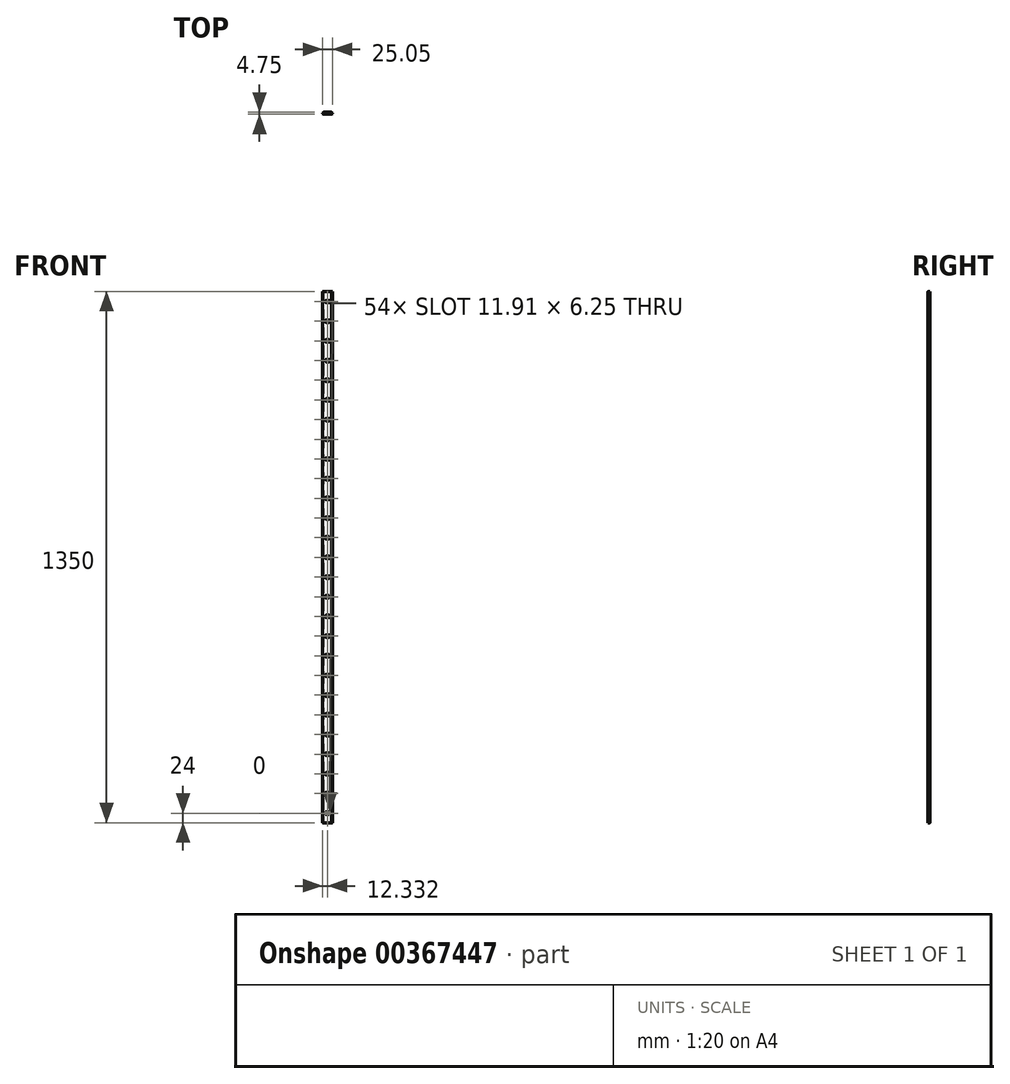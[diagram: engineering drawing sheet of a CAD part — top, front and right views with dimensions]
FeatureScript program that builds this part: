
annotation { "Feature Type Name" : "Feature", "Feature Type Description" : "" }
export const myFeature = defineFeature(function(context is Context, id is Id, definition is map)
    precondition{}
    {
        {
            var Q0;
            Q0=qCreatedBy(makeId("Top.planeOp"),FACE);
            var sketch = newSketch(context, id + "F0", { "sketchPlane" : qUnion([Q0])});
            skLineSegment(sketch, "E0", {"start": v(0, 0) * mm, "end": v(20.12, 0) * mm});
            skLineSegment(sketch, "E1", {"start": v(20.12, 0) * mm, "end": v(22.5, -2.37) * mm});
            skLineSegment(sketch, "E2", {"start": v(22.5, -2.37) * mm, "end": v(20.12, -4.75) * mm});
            skLineSegment(sketch, "E3", {"start": v(20.12, -4.75) * mm, "end": v(19.53, -4.75) * mm});
            skLineSegment(sketch, "E4", {"start": v(19.53, -4.75) * mm, "end": v(19.53, -2.37) * mm});
            skLineSegment(sketch, "E5", {"start": v(19.53, -2.37) * mm, "end": v(0, -2.38) * mm});
            skLineSegment(sketch, "E6", {"start": v(0, -2.38) * mm, "end": v(0, 0) * mm});
            skSolve(sketch);
        }
        {
            var Q0;
            Q0=qSketchRegion(id+"F0",true);
            extrude(context, id + "F1", {"entities" : qUnion([Q0]), "depth" : 1350 * mm});
        }
        {
            var Q0;
            Q0=makeQuery(id+"F1.opExtrude","SWEPT_EDGE",EDGE,{"disambiguationData":[OSD([sQuery(id+"F0.wireOp",EDGE,"E2"),sQuery(id+"F0.wireOp",EDGE,"E3")])]});
            var Q1;
            Q1=makeQuery(id+"F1.opExtrude","SWEPT_EDGE",EDGE,{"disambiguationData":[OSD([sQuery(id+"F0.wireOp",EDGE,"E1"),sQuery(id+"F0.wireOp",EDGE,"E2")])]});
            var Q2;
            Q2=makeQuery(id+"F1.opExtrude","SWEPT_EDGE",EDGE,{"disambiguationData":[OSD([sQuery(id+"F0.wireOp",EDGE,"E0"),sQuery(id+"F0.wireOp",EDGE,"E1")])]});
            fillet(context, id + "F2", {"entities" : qUnion([Q0, Q1, Q2]), "radius" : 0.5 * mm, "tangentPropagation" : true, "allowEdgeOverflow" : false});
        }
        {
            var Q0;
            Q0=makeQuery(id+"F1.opExtrude","SWEPT_BODY",BODY,{"disambiguationData":[OSD([sQuery(id+"F0.wireOp",EDGE,"E0"),sQuery(id+"F0.wireOp",EDGE,"E1"),sQuery(id+"F0.wireOp",EDGE,"E2"),sQuery(id+"F0.wireOp",EDGE,"E3"),sQuery(id+"F0.wireOp",EDGE,"E4"),sQuery(id+"F0.wireOp",EDGE,"E5"),sQuery(id+"F0.wireOp",EDGE,"E6")])]});
            var Q1;
            Q1=makeQuery(id+"F1.opExtrude","SWEPT_EDGE",EDGE,{"disambiguationData":[OSD([sQuery(id+"F0.wireOp",EDGE,"E5"),sQuery(id+"F0.wireOp",EDGE,"E6")])]});
            transform(context, id + "F3", {"entities" : qUnion([Q0]), "transformType" : TransformType.ROTATION, "transformAxis" : qUnion([Q1]), "angle" : 180 * degree, "makeCopy" : true});
        }
        {
            var Q0;
            Q0=makeQuery(id+"F3.opPattern","COPY",BODY,{"derivedFrom":makeQuery(id+"F1.opExtrude","SWEPT_BODY",BODY,{"disambiguationData":[OSD([sQuery(id+"F0.wireOp",EDGE,"E0"),sQuery(id+"F0.wireOp",EDGE,"E1"),sQuery(id+"F0.wireOp",EDGE,"E2"),sQuery(id+"F0.wireOp",EDGE,"E3"),sQuery(id+"F0.wireOp",EDGE,"E4"),sQuery(id+"F0.wireOp",EDGE,"E5"),sQuery(id+"F0.wireOp",EDGE,"E6")])]}),"instanceName":"1"});
            var Q1;
            Q1=makeQuery(id+"F3.opPattern","COPY",EDGE,{"derivedFrom":makeQuery(id+"F1.opExtrude","CAP_EDGE",EDGE,{"disambiguationData":[OSD([sQuery(id+"F0.wireOp",EDGE,"E5")])],"isStart":true}),"instanceName":"1"});
            transform(context, id + "F4", {"entities" : qUnion([Q0]), "transformType" : TransformType.TRANSLATION_ENTITY, "oppositeDirectionEntity" : false, "transformLine" : qUnion([Q1]), "makeCopy" : false});
        }
        {
            var Q0;
            Q0=makeQuery(id+"F3.opPattern","COPY",FACE,{"derivedFrom":makeQuery(id+"F1.opExtrude","SWEPT_FACE",FACE,{"disambiguationData":[OSD([sQuery(id+"F0.wireOp",EDGE,"E0")])]}),"instanceName":"1"});
            var sketch = newSketch(context, id + "F5", { "sketchPlane" : qUnion([Q0])});
            skLineSegment(sketch, "E7", {"start": v(9.57, 1350) * mm, "end": v(9.57, 1284.45) * mm, "construction": true});
            skLineSegment(sketch, "E8", {"start": v(-9.43, 1324) * mm, "end": v(34.24, 1324) * mm, "construction": true});
            skArc(sketch, "E9", {"start": v(9.57, 1322.68) * mm, "mid": v(15.04, 1322.32) * mm, "end": v(12.4, 1327.12) * mm});
            skArc(sketch, "E10", {"start": v(6.74, 1327.12) * mm, "mid": v(4.1, 1322.32) * mm, "end": v(9.57, 1322.68) * mm});
            skLineSegment(sketch, "E11", {"start": v(12.4, 1320.88) * mm, "end": v(6.74, 1320.88) * mm});
            skLineSegment(sketch, "E12", {"start": v(12.4, 1327.12) * mm, "end": v(6.74, 1327.12) * mm});
            skArc(sketch, "E13.0.1.0", {"start": v(6.74, 1277.12) * mm, "mid": v(4.1, 1272.32) * mm, "end": v(9.57, 1272.68) * mm});
            skLineSegment(sketch, "E13.0.1.1", {"start": v(12.4, 1270.88) * mm, "end": v(6.74, 1270.88) * mm});
            skArc(sketch, "E13.0.1.2", {"start": v(9.57, 1272.68) * mm, "mid": v(15.04, 1272.32) * mm, "end": v(12.4, 1277.12) * mm});
            skLineSegment(sketch, "E13.0.1.3", {"start": v(12.4, 1277.12) * mm, "end": v(6.74, 1277.12) * mm});
            skArc(sketch, "E13.0.2.0", {"start": v(6.74, 1227.13) * mm, "mid": v(4.1, 1222.32) * mm, "end": v(9.57, 1222.68) * mm});
            skLineSegment(sketch, "E13.0.2.1", {"start": v(12.4, 1220.88) * mm, "end": v(6.74, 1220.88) * mm});
            skArc(sketch, "E13.0.2.2", {"start": v(9.57, 1222.68) * mm, "mid": v(15.04, 1222.32) * mm, "end": v(12.4, 1227.13) * mm});
            skLineSegment(sketch, "E13.0.2.3", {"start": v(12.4, 1227.13) * mm, "end": v(6.74, 1227.13) * mm});
            skArc(sketch, "E13.0.3.0", {"start": v(6.74, 1177.13) * mm, "mid": v(4.1, 1172.32) * mm, "end": v(9.57, 1172.68) * mm});
            skLineSegment(sketch, "E13.0.3.1", {"start": v(12.4, 1170.88) * mm, "end": v(6.74, 1170.88) * mm});
            skArc(sketch, "E13.0.3.2", {"start": v(9.57, 1172.68) * mm, "mid": v(15.04, 1172.32) * mm, "end": v(12.4, 1177.13) * mm});
            skLineSegment(sketch, "E13.0.3.3", {"start": v(12.4, 1177.13) * mm, "end": v(6.74, 1177.13) * mm});
            skArc(sketch, "E13.0.4.0", {"start": v(6.74, 1127.13) * mm, "mid": v(4.1, 1122.32) * mm, "end": v(9.57, 1122.68) * mm});
            skLineSegment(sketch, "E13.0.4.1", {"start": v(12.4, 1120.88) * mm, "end": v(6.74, 1120.88) * mm});
            skArc(sketch, "E13.0.4.2", {"start": v(9.57, 1122.68) * mm, "mid": v(15.04, 1122.32) * mm, "end": v(12.4, 1127.13) * mm});
            skLineSegment(sketch, "E13.0.4.3", {"start": v(12.4, 1127.13) * mm, "end": v(6.74, 1127.13) * mm});
            skArc(sketch, "E13.0.5.0", {"start": v(6.74, 1077.13) * mm, "mid": v(4.1, 1072.32) * mm, "end": v(9.57, 1072.68) * mm});
            skLineSegment(sketch, "E13.0.5.1", {"start": v(12.4, 1070.88) * mm, "end": v(6.74, 1070.88) * mm});
            skArc(sketch, "E13.0.5.2", {"start": v(9.57, 1072.68) * mm, "mid": v(15.04, 1072.32) * mm, "end": v(12.4, 1077.13) * mm});
            skLineSegment(sketch, "E13.0.5.3", {"start": v(12.4, 1077.13) * mm, "end": v(6.74, 1077.13) * mm});
            skArc(sketch, "E13.0.6.0", {"start": v(6.74, 1027.13) * mm, "mid": v(4.1, 1022.32) * mm, "end": v(9.57, 1022.68) * mm});
            skLineSegment(sketch, "E13.0.6.1", {"start": v(12.4, 1020.88) * mm, "end": v(6.74, 1020.88) * mm});
            skArc(sketch, "E13.0.6.2", {"start": v(9.57, 1022.68) * mm, "mid": v(15.04, 1022.32) * mm, "end": v(12.4, 1027.13) * mm});
            skLineSegment(sketch, "E13.0.6.3", {"start": v(12.4, 1027.13) * mm, "end": v(6.74, 1027.13) * mm});
            skArc(sketch, "E13.0.7.0", {"start": v(6.74, 977.13) * mm, "mid": v(4.1, 972.32) * mm, "end": v(9.57, 972.68) * mm});
            skLineSegment(sketch, "E13.0.7.1", {"start": v(12.4, 970.88) * mm, "end": v(6.74, 970.88) * mm});
            skArc(sketch, "E13.0.7.2", {"start": v(9.57, 972.68) * mm, "mid": v(15.04, 972.32) * mm, "end": v(12.4, 977.13) * mm});
            skLineSegment(sketch, "E13.0.7.3", {"start": v(12.4, 977.13) * mm, "end": v(6.74, 977.13) * mm});
            skArc(sketch, "E13.0.8.0", {"start": v(6.74, 927.13) * mm, "mid": v(4.1, 922.32) * mm, "end": v(9.57, 922.68) * mm});
            skLineSegment(sketch, "E13.0.8.1", {"start": v(12.4, 920.88) * mm, "end": v(6.74, 920.88) * mm});
            skArc(sketch, "E13.0.8.2", {"start": v(9.57, 922.68) * mm, "mid": v(15.04, 922.32) * mm, "end": v(12.4, 927.13) * mm});
            skLineSegment(sketch, "E13.0.8.3", {"start": v(12.4, 927.13) * mm, "end": v(6.74, 927.13) * mm});
            skArc(sketch, "E13.0.9.0", {"start": v(6.74, 877.13) * mm, "mid": v(4.1, 872.32) * mm, "end": v(9.57, 872.68) * mm});
            skLineSegment(sketch, "E13.0.9.1", {"start": v(12.4, 870.88) * mm, "end": v(6.74, 870.88) * mm});
            skArc(sketch, "E13.0.9.2", {"start": v(9.57, 872.68) * mm, "mid": v(15.04, 872.32) * mm, "end": v(12.4, 877.13) * mm});
            skLineSegment(sketch, "E13.0.9.3", {"start": v(12.4, 877.13) * mm, "end": v(6.74, 877.13) * mm});
            skArc(sketch, "E13.0.10.0", {"start": v(6.74, 827.13) * mm, "mid": v(4.1, 822.32) * mm, "end": v(9.57, 822.68) * mm});
            skLineSegment(sketch, "E13.0.10.1", {"start": v(12.4, 820.88) * mm, "end": v(6.74, 820.88) * mm});
            skArc(sketch, "E13.0.10.2", {"start": v(9.57, 822.68) * mm, "mid": v(15.04, 822.32) * mm, "end": v(12.4, 827.13) * mm});
            skLineSegment(sketch, "E13.0.10.3", {"start": v(12.4, 827.13) * mm, "end": v(6.74, 827.13) * mm});
            skArc(sketch, "E13.0.11.0", {"start": v(6.74, 777.13) * mm, "mid": v(4.1, 772.32) * mm, "end": v(9.57, 772.68) * mm});
            skLineSegment(sketch, "E13.0.11.1", {"start": v(12.4, 770.88) * mm, "end": v(6.74, 770.88) * mm});
            skArc(sketch, "E13.0.11.2", {"start": v(9.57, 772.68) * mm, "mid": v(15.04, 772.32) * mm, "end": v(12.4, 777.13) * mm});
            skLineSegment(sketch, "E13.0.11.3", {"start": v(12.4, 777.13) * mm, "end": v(6.74, 777.13) * mm});
            skArc(sketch, "E13.0.12.0", {"start": v(6.74, 727.13) * mm, "mid": v(4.1, 722.32) * mm, "end": v(9.57, 722.68) * mm});
            skLineSegment(sketch, "E13.0.12.1", {"start": v(12.4, 720.88) * mm, "end": v(6.74, 720.88) * mm});
            skArc(sketch, "E13.0.12.2", {"start": v(9.57, 722.68) * mm, "mid": v(15.04, 722.32) * mm, "end": v(12.4, 727.13) * mm});
            skLineSegment(sketch, "E13.0.12.3", {"start": v(12.4, 727.13) * mm, "end": v(6.74, 727.13) * mm});
            skArc(sketch, "E13.0.13.0", {"start": v(6.74, 677.13) * mm, "mid": v(4.1, 672.32) * mm, "end": v(9.57, 672.68) * mm});
            skLineSegment(sketch, "E13.0.13.1", {"start": v(12.4, 670.88) * mm, "end": v(6.74, 670.88) * mm});
            skArc(sketch, "E13.0.13.2", {"start": v(9.57, 672.68) * mm, "mid": v(15.04, 672.32) * mm, "end": v(12.4, 677.13) * mm});
            skLineSegment(sketch, "E13.0.13.3", {"start": v(12.4, 677.13) * mm, "end": v(6.74, 677.13) * mm});
            skArc(sketch, "E13.0.14.0", {"start": v(6.74, 627.13) * mm, "mid": v(4.1, 622.32) * mm, "end": v(9.57, 622.68) * mm});
            skLineSegment(sketch, "E13.0.14.1", {"start": v(12.4, 620.88) * mm, "end": v(6.74, 620.88) * mm});
            skArc(sketch, "E13.0.14.2", {"start": v(9.57, 622.68) * mm, "mid": v(15.04, 622.32) * mm, "end": v(12.4, 627.13) * mm});
            skLineSegment(sketch, "E13.0.14.3", {"start": v(12.4, 627.13) * mm, "end": v(6.74, 627.13) * mm});
            skArc(sketch, "E13.0.15.0", {"start": v(6.74, 577.13) * mm, "mid": v(4.1, 572.32) * mm, "end": v(9.57, 572.68) * mm});
            skLineSegment(sketch, "E13.0.15.1", {"start": v(12.4, 570.88) * mm, "end": v(6.74, 570.88) * mm});
            skArc(sketch, "E13.0.15.2", {"start": v(9.57, 572.68) * mm, "mid": v(15.04, 572.32) * mm, "end": v(12.4, 577.13) * mm});
            skLineSegment(sketch, "E13.0.15.3", {"start": v(12.4, 577.13) * mm, "end": v(6.74, 577.13) * mm});
            skArc(sketch, "E13.0.16.0", {"start": v(6.74, 527.13) * mm, "mid": v(4.1, 522.32) * mm, "end": v(9.57, 522.68) * mm});
            skLineSegment(sketch, "E13.0.16.1", {"start": v(12.4, 520.88) * mm, "end": v(6.74, 520.88) * mm});
            skArc(sketch, "E13.0.16.2", {"start": v(9.57, 522.68) * mm, "mid": v(15.04, 522.32) * mm, "end": v(12.4, 527.13) * mm});
            skLineSegment(sketch, "E13.0.16.3", {"start": v(12.4, 527.13) * mm, "end": v(6.74, 527.13) * mm});
            skArc(sketch, "E13.0.17.0", {"start": v(6.74, 477.13) * mm, "mid": v(4.1, 472.32) * mm, "end": v(9.57, 472.68) * mm});
            skLineSegment(sketch, "E13.0.17.1", {"start": v(12.4, 470.88) * mm, "end": v(6.74, 470.88) * mm});
            skArc(sketch, "E13.0.17.2", {"start": v(9.57, 472.68) * mm, "mid": v(15.04, 472.32) * mm, "end": v(12.4, 477.13) * mm});
            skLineSegment(sketch, "E13.0.17.3", {"start": v(12.4, 477.13) * mm, "end": v(6.74, 477.13) * mm});
            skArc(sketch, "E13.0.18.0", {"start": v(6.74, 427.13) * mm, "mid": v(4.1, 422.32) * mm, "end": v(9.57, 422.68) * mm});
            skLineSegment(sketch, "E13.0.18.1", {"start": v(12.4, 420.88) * mm, "end": v(6.74, 420.88) * mm});
            skArc(sketch, "E13.0.18.2", {"start": v(9.57, 422.68) * mm, "mid": v(15.04, 422.32) * mm, "end": v(12.4, 427.13) * mm});
            skLineSegment(sketch, "E13.0.18.3", {"start": v(12.4, 427.13) * mm, "end": v(6.74, 427.13) * mm});
            skArc(sketch, "E13.0.19.0", {"start": v(6.74, 377.13) * mm, "mid": v(4.1, 372.32) * mm, "end": v(9.57, 372.68) * mm});
            skLineSegment(sketch, "E13.0.19.1", {"start": v(12.4, 370.88) * mm, "end": v(6.74, 370.88) * mm});
            skArc(sketch, "E13.0.19.2", {"start": v(9.57, 372.68) * mm, "mid": v(15.04, 372.32) * mm, "end": v(12.4, 377.13) * mm});
            skLineSegment(sketch, "E13.0.19.3", {"start": v(12.4, 377.13) * mm, "end": v(6.74, 377.13) * mm});
            skLineSegment(sketch, "E13.direction1", {"start": v(6.74, 1320.88) * mm, "end": v(-20.5, 1325.4) * mm, "construction": true});
            skLineSegment(sketch, "E13.direction2", {"start": v(6.74, 1320.88) * mm, "end": v(6.74, 1270.88) * mm, "construction": true});
            skArc(sketch, "E14.0.0.20", {"start": v(6.74, 327.13) * mm, "mid": v(4.1, 322.32) * mm, "end": v(9.57, 322.68) * mm});
            skLineSegment(sketch, "E14.4.0.20", {"start": v(12.4, 320.88) * mm, "end": v(6.74, 320.88) * mm});
            skArc(sketch, "E14.7.0.20", {"start": v(9.57, 322.68) * mm, "mid": v(15.04, 322.32) * mm, "end": v(12.4, 327.13) * mm});
            skLineSegment(sketch, "E14.11.0.20", {"start": v(12.4, 327.13) * mm, "end": v(6.74, 327.13) * mm});
            skArc(sketch, "E14.0.0.21", {"start": v(6.74, 277.13) * mm, "mid": v(4.1, 272.32) * mm, "end": v(9.57, 272.68) * mm});
            skLineSegment(sketch, "E14.4.0.21", {"start": v(12.4, 270.88) * mm, "end": v(6.74, 270.88) * mm});
            skArc(sketch, "E14.7.0.21", {"start": v(9.57, 272.68) * mm, "mid": v(15.04, 272.32) * mm, "end": v(12.4, 277.13) * mm});
            skLineSegment(sketch, "E14.11.0.21", {"start": v(12.4, 277.13) * mm, "end": v(6.74, 277.13) * mm});
            skArc(sketch, "E14.0.0.22", {"start": v(6.74, 227.13) * mm, "mid": v(4.1, 222.32) * mm, "end": v(9.57, 222.68) * mm});
            skLineSegment(sketch, "E14.4.0.22", {"start": v(12.4, 220.88) * mm, "end": v(6.74, 220.88) * mm});
            skArc(sketch, "E14.7.0.22", {"start": v(9.57, 222.68) * mm, "mid": v(15.04, 222.32) * mm, "end": v(12.4, 227.13) * mm});
            skLineSegment(sketch, "E14.11.0.22", {"start": v(12.4, 227.13) * mm, "end": v(6.74, 227.13) * mm});
            skArc(sketch, "E14.0.0.23", {"start": v(6.74, 177.13) * mm, "mid": v(4.1, 172.32) * mm, "end": v(9.57, 172.68) * mm});
            skLineSegment(sketch, "E14.4.0.23", {"start": v(12.4, 170.88) * mm, "end": v(6.74, 170.88) * mm});
            skArc(sketch, "E14.7.0.23", {"start": v(9.57, 172.68) * mm, "mid": v(15.04, 172.32) * mm, "end": v(12.4, 177.13) * mm});
            skLineSegment(sketch, "E14.11.0.23", {"start": v(12.4, 177.13) * mm, "end": v(6.74, 177.13) * mm});
            skArc(sketch, "E14.0.0.24", {"start": v(6.74, 127.13) * mm, "mid": v(4.1, 122.32) * mm, "end": v(9.57, 122.68) * mm});
            skLineSegment(sketch, "E14.4.0.24", {"start": v(12.4, 120.88) * mm, "end": v(6.74, 120.88) * mm});
            skArc(sketch, "E14.7.0.24", {"start": v(9.57, 122.68) * mm, "mid": v(15.04, 122.32) * mm, "end": v(12.4, 127.13) * mm});
            skLineSegment(sketch, "E14.11.0.24", {"start": v(12.4, 127.13) * mm, "end": v(6.74, 127.13) * mm});
            skArc(sketch, "E14.0.0.25", {"start": v(6.74, 77.13) * mm, "mid": v(4.1, 72.32) * mm, "end": v(9.57, 72.68) * mm});
            skLineSegment(sketch, "E14.4.0.25", {"start": v(12.4, 70.88) * mm, "end": v(6.74, 70.88) * mm});
            skArc(sketch, "E14.7.0.25", {"start": v(9.57, 72.68) * mm, "mid": v(15.04, 72.32) * mm, "end": v(12.4, 77.13) * mm});
            skLineSegment(sketch, "E14.11.0.25", {"start": v(12.4, 77.13) * mm, "end": v(6.74, 77.13) * mm});
            skArc(sketch, "E14.0.0.26", {"start": v(6.74, 27.13) * mm, "mid": v(4.1, 22.32) * mm, "end": v(9.57, 22.68) * mm});
            skLineSegment(sketch, "E14.4.0.26", {"start": v(12.4, 20.88) * mm, "end": v(6.74, 20.88) * mm});
            skArc(sketch, "E14.7.0.26", {"start": v(9.57, 22.68) * mm, "mid": v(15.04, 22.32) * mm, "end": v(12.4, 27.13) * mm});
            skLineSegment(sketch, "E14.11.0.26", {"start": v(12.4, 27.13) * mm, "end": v(6.74, 27.13) * mm});
            skArc(sketch, "E14.0.0.27", {"start": v(6.74, -22.87) * mm, "mid": v(4.1, -27.68) * mm, "end": v(9.57, -27.32) * mm});
            skLineSegment(sketch, "E14.4.0.27", {"start": v(12.4, -29.12) * mm, "end": v(6.74, -29.12) * mm});
            skArc(sketch, "E14.7.0.27", {"start": v(9.57, -27.32) * mm, "mid": v(15.04, -27.68) * mm, "end": v(12.4, -22.87) * mm});
            skLineSegment(sketch, "E14.11.0.27", {"start": v(12.4, -22.87) * mm, "end": v(6.74, -22.87) * mm});
            skArc(sketch, "E14.0.0.28", {"start": v(6.74, -72.87) * mm, "mid": v(4.1, -77.68) * mm, "end": v(9.57, -77.32) * mm});
            skLineSegment(sketch, "E14.4.0.28", {"start": v(12.4, -79.12) * mm, "end": v(6.74, -79.12) * mm});
            skArc(sketch, "E14.7.0.28", {"start": v(9.57, -77.32) * mm, "mid": v(15.04, -77.68) * mm, "end": v(12.4, -72.87) * mm});
            skLineSegment(sketch, "E14.11.0.28", {"start": v(12.4, -72.87) * mm, "end": v(6.74, -72.87) * mm});
            skArc(sketch, "E14.0.0.29", {"start": v(6.74, -122.87) * mm, "mid": v(4.1, -127.68) * mm, "end": v(9.57, -127.32) * mm});
            skLineSegment(sketch, "E14.4.0.29", {"start": v(12.4, -129.12) * mm, "end": v(6.74, -129.12) * mm});
            skArc(sketch, "E14.7.0.29", {"start": v(9.57, -127.32) * mm, "mid": v(15.04, -127.68) * mm, "end": v(12.4, -122.87) * mm});
            skLineSegment(sketch, "E14.11.0.29", {"start": v(12.4, -122.87) * mm, "end": v(6.74, -122.87) * mm});
            skSolve(sketch);
        }
        {
            var Q0;
            Q0=qSketchRegion(id+"F5",true);
            extrude(context, id + "F6", {"entities" : qUnion([Q0]), "operationType" : NewBodyOperationType.REMOVE, "oppositeDirection" : true, "depth" : 25 * mm});
        }
    });
